# Revit family: Domotics-DomesticRanges-GEWISS-SYSTEM_COMMAND-ONE-WAY_SWITCH
name_source: partatom
category: Apparecchi elettrici
revit_build: Autodesk Revit 2016 (Build: 20161004_0715(x64)
units: mm (PartAtom-declared; Revit-internal decimal feet)

## family parameters
Condiviso = Sì
Host = Superficie
Mantenere orientamento annotazione = Sì
Numero OmniClass = 23.80.50.11.14
Punto di calcolo locali = Sì
Quota connettore circolare = Usa diametro
Taglio con vuoti quando caricato = No
Tipo di parte = Normale
Titolo OmniClass = Switches

## types (12) — shared parameters
Catalogue = DOMOTICS
Catalogue Range = SYSTEM - DOMESTIC RANGE
Electrocod = 0130
IDF = f46078f3-fac7-4de0-893f-0ca9abbc7cad
IDT = 4b516810-c773-4bee-a753-a575d61c2f19
Immagine tipo = GW21584.jpg
Produttore = GEWISS S.p.A.
Prospetto di default = 1219 mm
Simboli accensione interruttore = No
Simbolo_int = SIMBOLO INTERRUTTORI : INT2PLUM
Technical sheet = https://www.gewiss.com
Tipo_int = SYSTEM INTERRUTTORI_BASE : GW21584 - INTERRUTTORE 2P 16A ILLUMINABILE SY/BK
URL = https://www.gewiss.com
Version file RFA = 19.4
Vetrino luminoso = Sì

## per-type parameters (varying)
| type | Button key | Characteristics | Colour | Description. | Description: | Descrizione | EAN code | Modello | No. SYSTEM modules | SEO | Type | Typology | Voltage | Voltage: |
| GW20572 - Switch-1P 16Ax lumin.230V white | With replaceable neutral lens | 1P - 16AX | White | Switch | 1P - 16 AX backlit | SWITCH-1P 16AX LUMIN.230V SY/WT | 8011564132931 | GW20572 | 1 | 1 way switch | Backlit 230V ac (0.4W) | Backlit 230V ac (0.4W) | 250 V ac | 250 V ac |
| GW21503 - SWITCH-2P 16A SY/BK |  |  |  |  |  | SWITCH-2P 16A SY/BK | 8011564127951 | GW21503 |  |  |  |  |  |  |
| GW20583 - Switch-1P 16Ax illuminable white | With replaceable neutral lens | 1P - 16AX | White | Switch | 1P - 16AX illuminable | SWITCH-1P 16AX ILLUMINABLE SY/WT | 8011564132948 | GW20583 | 1 | 1 way switch | Illuminable | Illuminable | 250 V ac | 250 V ac |
| GW21583 - SWITCH-1P 16AX ILLUMINABLE SY/BK |  |  |  |  |  | SWITCH-1P 16AX ILLUMINABLE SY/BK | 8011564133037 | GW21583 |  |  |  |  |  |  |
| GW21584 - SWITCH-2P 16A ILLUMINABLE SY/BK |  |  |  |  |  | SWITCH-2P 16A ILLUMINABLE SY/BK | 8011564127975 | GW21584 |  |  |  |  |  |  |
| GW20503 - Switch-2P 16A white | Neutral | 2P - 16 AX | White | One-way switch 2P - 16AX | 2P - 16 AX | SWITCH-2P 16A SY/WT | 8011564077201 | GW20503 | 1 | 1 way switch | General | General | 250 V ac | 250 V ac |
| GW21572 - SWITCH-1P 16AX LUMIN.230V SY/BK |  |  |  |  |  | SWITCH-1P 16AX LUMIN.230V SY/BK | 8011564133020 | GW21572 |  |  |  |  |  |  |
| GW21571 - SWITCH-1P 16AX SY/BK |  |  |  |  |  | SWITCH-1P 16AX SY/BK | 8011564133013 | GW21571 |  |  |  |  |  |  |
| GW20504 - Switch-2P 16A luminous 230V white | With replaceable neutral lens | 2P - 16 AX | White | Switch | 2P - 16 AX backlit | SWITCH-2P 16A LUMINOUS 230V SY/WT | 8011564077218 | GW20504 | 1 | 1 way switch | Backlit 230V ac (0.4W) | Backlit 230V ac (0.4W) | 250 V ac | 250 V ac |
| GW21504 - SWITCH-2P 16A LUMINOUS 230V SY/BK |  |  |  |  |  | SWITCH-2P 16A LUMINOUS 230V SY/BK | 8011564127968 | GW21504 |  |  |  |  |  |  |
| GW20571 - Switch-1P 16Ax white | Neutral | 1P - 16AX | White | Switch | 1P - 16AX | SWITCH-1P 16AX SY/WT | 8011564132924 | GW20571 | 1 | 1 way switch | General | General | 250 V ac | 250 V ac |
| GW20584 - Switch-2P 16A illuminable white | With replaceable neutral lens | 2P - 16 AX | White | Switch | 2P - 16AX illuminable | SWITCH-2P 16A ILLUMINABLE SY/WT | 8011564079496 | GW20584 | 1 | 1 way switch | Illuminable | Illuminable | 250 V ac | 250 V ac |

## geometry (parser evidence)
native form markers: Sweep x2
no freeform markers — native parametric forms only
